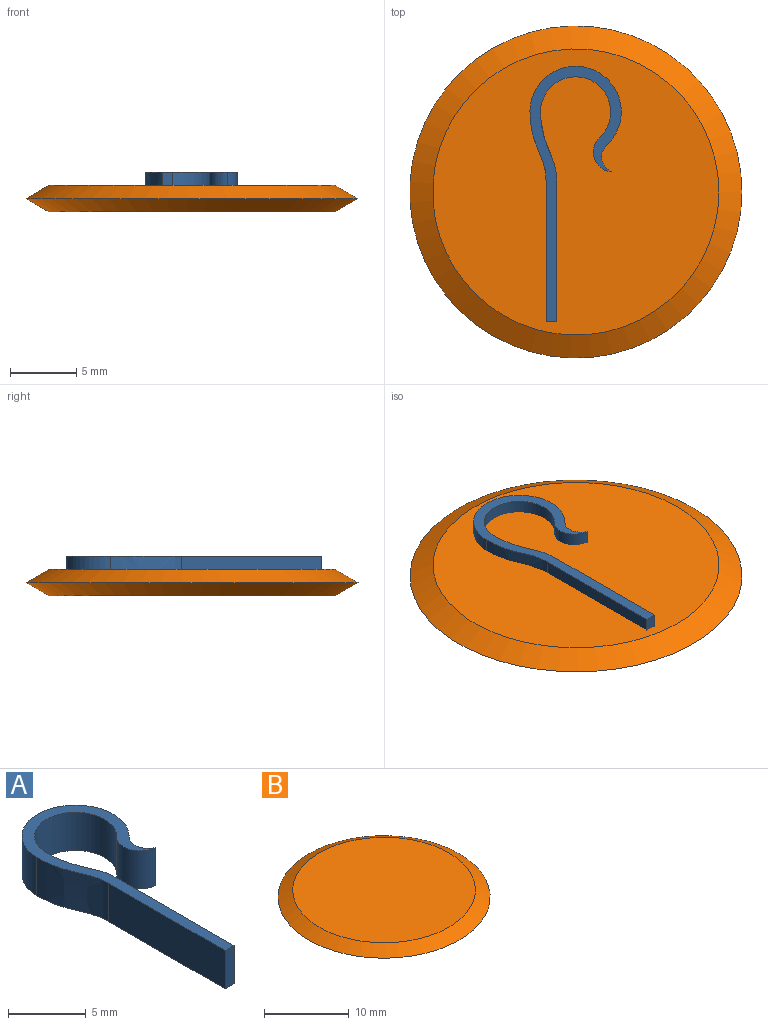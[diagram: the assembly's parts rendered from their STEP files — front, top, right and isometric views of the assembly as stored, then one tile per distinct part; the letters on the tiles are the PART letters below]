
ASSEMBLY  parts=2 mates=1
PART A: 11 faces, bbox 6.9x19.2x3 mm
  f0: cylinder r=3.44mm len=6.88mm, axis (0,0,-1), area 40.6mm2, adj f1,f8,f9,f10
  f1: extruded ~5.31x3mm, area 16.5mm2, adj f0,f2,f9,f10
  f2: plane 10.6x3mm, normal (-1,0,0), area 31.8mm2, adj f1,f3,f9,f10
  f3: plane 3x0.8mm, normal (0,-1,0), area 2.4mm2, adj f2,f4,f9,f10
  f4: plane 10.6x3mm, normal (1,0,0), area 31.8mm2, adj f3,f5,f9,f10
  f5: extruded ~5.31x3mm, area 16.5mm2, adj f4,f6,f9,f10
  f6: cylinder r=2.64mm len=5.28mm, axis (0,0,-1), area 31.1mm2, adj f5,f7,f9,f10
  f7: cylinder r=1.5mm len=3mm, axis (0,0,-1), area 10.4mm2, adj f6,f8,f9,f10
  f8: cylinder r=1.21mm len=3mm, axis (0,0,-1), area 7.2mm2, adj f0,f7,f9,f10
  f9: plane 19.25x6.88mm, normal (0,0,1), area 23.7mm2, adj f0,f1,f2,f3,f4,f5,f6,f7
  f10: plane 19.25x6.88mm, normal (0,0,-1), area 23.7mm2, adj f0,f1,f2,f3,f4,f5,f6,f7
PART B: 4 faces, bbox 25x25x2 mm
  f0: plane 21.54x21.54mm, normal (0,0,1), area 364.3mm2, adj f1
  f1: cone r=12.5mm half-angle=60deg, axis (0,0,-1), area 146.2mm2, adj f0,f2
  f2: cone r=12.5mm half-angle=60deg, axis (0,0,1), area 146.2mm2, adj f1,f3
  f3: plane 21.54x21.54mm, normal (0,0,-1), area 364.3mm2, adj f2
PLACE A at identity
PLACE B at identity
MATE fastened A.f10 <-> B.f1  axis (0,0,-1) through (0,0,-1)mm
